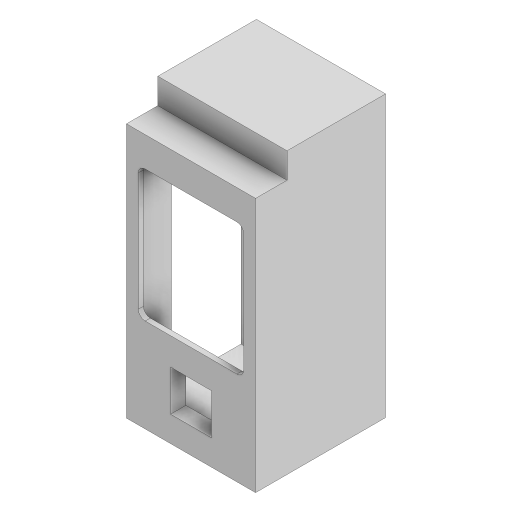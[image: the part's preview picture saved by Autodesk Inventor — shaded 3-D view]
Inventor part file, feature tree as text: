
AUTODESK INVENTOR PART (.ipt)
format: ipt  version: 2023.3 (Build 273359000, 359)  size: 663,040 bytes
history: native  units: mm
features: extrude x19, sketch x17, projected_geometry x6, fillet x2, chamfer x1
ambient origin geometry x8: Origin, YZ Plane, XZ Plane, XY Plane, X Axis, Y Axis, Z Axis, Center Point
bodies: Solid1 (feature_tree)
feature tree (45):
  sketch  "Sketch1"  dims[d0=34.0mm d1=45.0mm]
  extrude  "Extrusion1"  Depth=45.0mm
  extrude  "Extrusion2"  Depth=12.0mm
  fillet  "Fillet1"  Radius=12.0mm
  extrude  "Extrusion3"  Depth=34.0mm
  extrude  "Extrusion4"  Depth=13.0mm
  extrude  "Extrusion5"  Depth=3.0mm
  extrude  "Extrusion6"  Depth=3.0mm
  extrude  "Extrusion7"  Depth=28.25mm
  extrude  "Extrusion8"  Depth=3.0mm
  extrude  "Extrusion9"  Depth=2.0mm
  fillet  "Fillet2"  Radius=2.0mm
  extrude  "Extrusion10"  Depth=2.0mm
  chamfer  "Chamfer1"  Distance=4.5mm
  sketch  "Sketch10"  dims[d22=2.0mm d23=2.0mm d24=4.5mm d25=0.0mm]
  extrude  "Extrusion11"  Depth=1.5mm
  extrude  "Extrusion12"  Depth=5.5mm
  extrude  "Extrusion14"  Depth=2.0mm
  extrude  "Extrusion13"  Depth=22.5mm
  sketch  "Sketch13"  dims[d30=1.5mm d31=0.0mm d32=2.0mm]
  extrude  "Extrusion15"  Depth=2.0mm TaperAngle=0.0deg
  extrude  "Extrusion16"  Depth=2.0mm TaperAngle=0.0deg
  extrude  "Extrusion17"  Depth=10.0mm TaperAngle=0.0deg
  extrude  "Extrusion18"  Depth=10.0mm TaperAngle=0.0deg
  extrude  "Extrusion19"  Depth=2.15mm
  sketch  "Sketch2"  dims[d2=2.5mm d3=12.0mm d4=12.0mm]
  sketch  "Sketch3"  dims[d5=34.0mm d6=58.0mm]
  sketch  "Sketch4"  dims[d7=7.0mm d8=13.0mm]
  sketch  "Sketch5"  dims[d9=29.0mm d10=3.0mm]
  sketch  "Sketch6"  dims[d11=3.0mm d12=3.0mm]
  sketch  "Sketch7"  dims[d13=3.0mm d14=28.25mm d15=14.125mm]
  sketch  "Sketch8"  dims[d16=3.0mm d17=24.0mm]
  sketch  "Sketch9"  dims[d18=12.0mm d19=2.62mm d21=2.0mm]
  sketch  "Sketch11"  dims[d26=0.75mm d27=1.5mm]
  sketch  "Sketch12"  dims[d28=1.5mm d29=5.5mm]
  projected_geometry  "Projected Loop1"
  sketch  "Sketch14"  dims[d33=29.25mm d34=0.0mm d35=22.5mm]
  sketch  "Sketch15"  dims[d36=29.25mm d37=0.0mm d38=2.0mm d39=0.0mm]
  projected_geometry  "Projected Loop2"
  sketch  "Sketch16"  dims[d40=7.5mm d41=2.0mm d42=0.0mm]
  projected_geometry  "Projected Loop3"
  sketch  "Sketch17"  dims[d43=2.0mm d44=10.0mm d45=0.0mm d46=10.0mm d47=0.0mm d48=2.15mm d49=3.6mm d50=9.25mm d51=10.0mm d52=0.0mm d53=0.75mm d54=4.8mm d55=39.25mm d56=10.65mm d57=1.0mm d58=3.0mm d59=0.0mm d61=2.0mm d62=2.0mm d63=45.0deg d64=3.732763mm d65=3.732763mm d66=4.8mm d67=4.8mm d68=4.8mm d69=4.8mm d70=3.0mm d71=0.0mm d72=5.8mm d73=2.7mm d74=1.0mm d75=5.5mm d76=10.0mm d77=0.0mm d78=5.5mm d79=10.0mm d80=0.0mm d81=5.8mm d82=2.7mm d83=1.0mm d85=5.5mm d86=5.8mm d87=2.7mm d88=1.0mm d89=10.0mm d90=0.0mm d91=10.0mm d92=0.0mm d93=10.0mm d94=0.0mm d95=3.2mm d96=3.2mm d97=10.0mm d98=0.0mm d99=6.4mm d100=6.4mm d101=2.5mm d102=0.0mm d103=1.5mm d104=0.0mm]
  projected_geometry  "Projected Loop4"
  projected_geometry  "Projected Loop5"
  projected_geometry  "Projected Loop6"
